# Revit family: Domotics-DomesticRanges-GEWISS-CHORUS_COMMAND-INTERMEDIATE_SWITCH_1M
name_source: partatom
category: Apparecchi elettrici
revit_build: Autodesk Revit 2016 (Build: 20161004_0715(x64)
units: mm (PartAtom-declared; Revit-internal decimal feet)

## family parameters
Condiviso = Sì
Host = Superficie
Mantenere orientamento annotazione = Sì
Numero OmniClass = 23.80.50.11.14
Punto di calcolo locali = No
Quota connettore circolare = Usa diametro
Taglio con vuoti quando caricato = Sì
Tipo di parte = Normale
Titolo OmniClass = Switches

## types (9) — shared parameters
Bidimensionale = bidimensionale invertitori 1m : GW12093
Breaking capacity: = 1.25 In (200 position changes)
Carico apparente = 0 VA
Catalogue = DOMOTICS
Catalogue Range = CHORUS - DOMESTIC RANGE
Category = Reversing switch
Electrocod = 0130
Glow Wire Test = 850°C
IDF = e6ea1d11-b10b-4c80-9ee7-46acade47ee4
IDT = 8ec74ef9-a541-4a1d-80cc-bf3e3b74c129
Immagine tipo = GW14093.jpg
Insulation resistance = > 5 MOhm
Larghezza pulsante = 23 mm  [stored 0.0754593 ft]
N. poli = 1
No. Chorus modules = 1
Number of poles = 1P
Produttore = GEWISS S.p.A.
Prolonged operation (no.of position changes) = 40.000 at In 250 V ac cosÃ˜=0,6
Prospetto di default = 1219 mm
Resistance at test voltage = 2000 V at 50 Hz for 1 minute
SEO = Intermediate switch
Simbolo = SIMBOLO INVERTITORI : INV1PLUM
Standard; = EN 60669-1
Technical sheet = https://www.gewiss.com
Terminal grip on cable traction = > 50 N
Terminal tightening capacity flexible cables (mm2) = min. 0,75 - max. 2x4
Terminal tightening capacity rigid cables (mm2) = min. 0,5 - max. 2x2,5
Thermo-pressure with ball = 125
Tipo_ = CHORUS INVERTITORI 1M_BASE : GW14093 - Titanio - Illuminabile segnalazione
URL = https://www.gewiss.com
Version file RFA = 19.0
Volt = 230 V
Voltage = 250 V ac
Voltage: = 250 V ac
Wiring terminals = With screw

## per-type parameters (varying)
| type | Button key | Colour | Description: | Descrizione | EAN code | Modello | Type |
| GW10092 - White - Illuminable | With diffuser | White | 1P - 16AX illuminable | REV.SWITCH, 1M 1P 16AX ILL LOC WHITE | 8011564258235 | GW10092 | Backlit |
| GW14093 - Titanium - Illuminable | With replaceable neutral lens | Titanium | 1P - 16AX illuminable | REV.SWITCH 1M 1P 16AX ILL SIG TITANIUM | 8011564265721 | GW14093 | Indicator |
| GW10091 - White | Neutral | White | 1P - 16AX | REVERSING SWITCH, 1M 1P 16AX WHITE | 8011564258228 | GW10091 | General |
| GW14091 - Titanium | Neutral | Titanium | 1P - 16AX | REVERSING SWITCH, 1M 1P 16AX TITANIUM | 8011564265707 | GW14091 | General |
| GW10093 - White - Illuminable | With replaceable neutral lens | White | 1P - 16AX illuminable | REV.SWITCH, 1M 1P 16AX ILL SIG WHITE | 8011564258242 | GW10093 | Indicator |
| GW14092 - Titanium - Illuminable | With diffuser | Titanium | 1P - 16AX illuminable | REV.SWITCH 1M 1P 16AX ILL LOC TITANIUM | 8011564265714 | GW14092 | Backlit |
| GW12093 - Black - Illuminable | With replaceable neutral lens | Black | 1P - 16AX illuminable | REV.SWITCH, 1M 1P 16AX ILL SIG BLACK | 8011564267152 | GW12093 | Indicator |
| GW12091 - Black | Neutral | Black | 1P - 16AX | REVERSING SWITCH, 1M 1P 16AX BLACK | 8011564267138 | GW12091 | General |
| GW12092 - Black - Illuminable | With diffuser | Black | 1P - 16AX illuminable | REV.SWITCH, 1M 1P 16AX ILL LOC BLACK | 8011564267145 | GW12092 | Backlit |

note: source unit labels omitted for Thermo-pressure with ball — the stored unit's dimension contradicts the parameter name (converter mislabeling)

note: [stored X ft] marks values corroborated as IEEE doubles in the binary element streams (Revit-internal decimal feet)

## geometry (parser evidence)
native form markers: Sweep x2
no freeform markers — native parametric forms only
